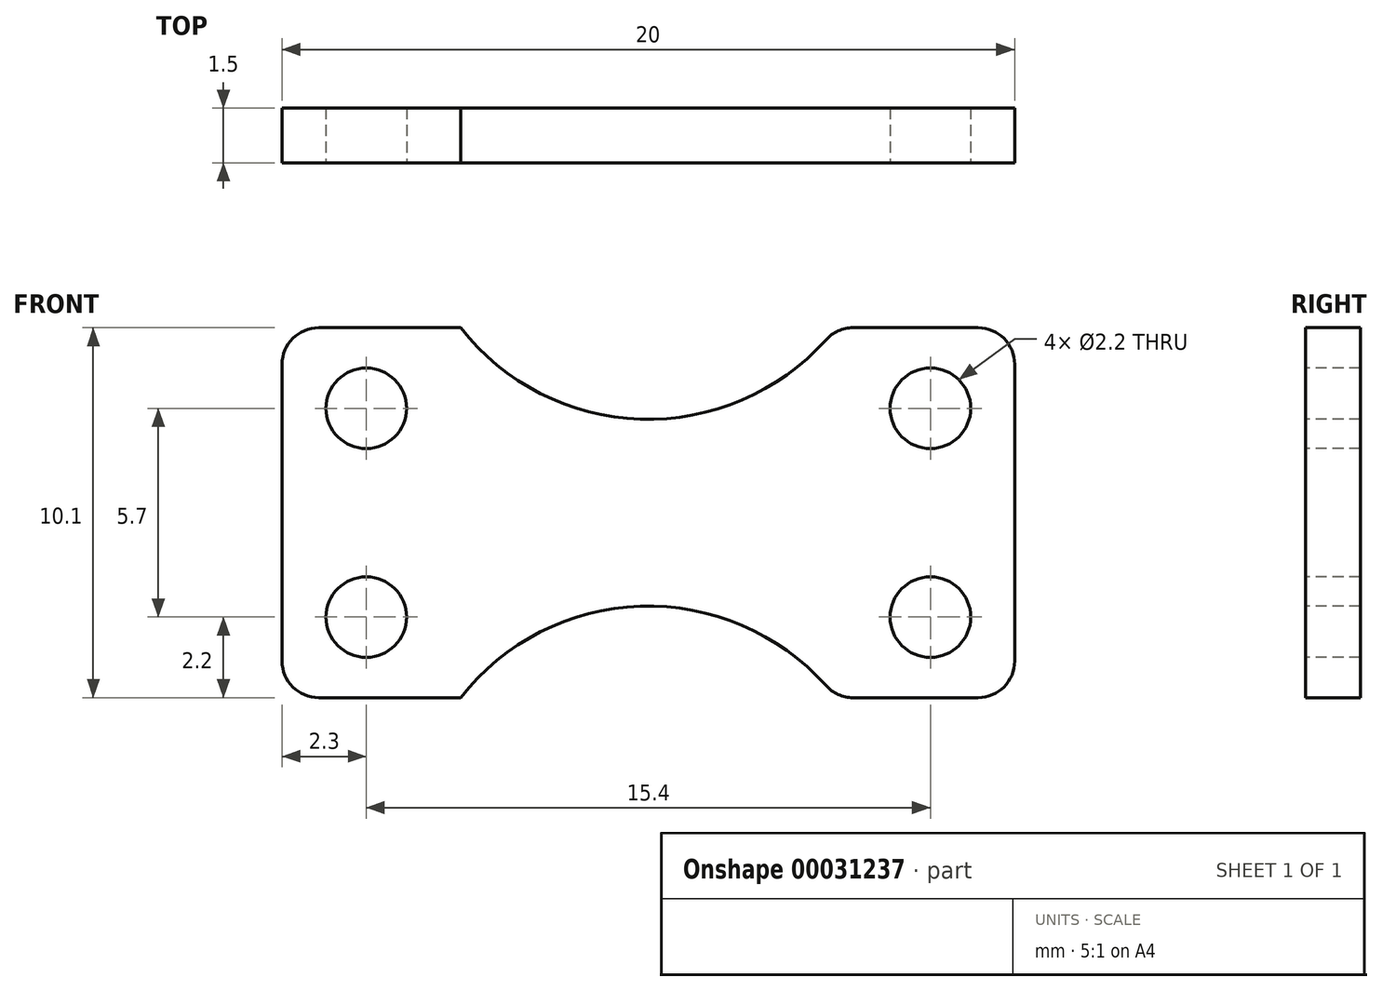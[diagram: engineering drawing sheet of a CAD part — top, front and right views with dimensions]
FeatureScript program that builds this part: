
annotation { "Feature Type Name" : "Feature", "Feature Type Description" : "" }
export const myFeature = defineFeature(function(context is Context, id is Id, definition is map)
    precondition{}
    {
        {
            var Q0;
            Q0=qCreatedBy(makeId("Front.planeOp"),FACE);
            var sketch = newSketch(context, id + "F0", { "sketchPlane" : qUnion([Q0])});
            skLineSegment(sketch, "E0.bottom", {"start": v(0, 0) * mm, "end": v(20, 0) * mm});
            skLineSegment(sketch, "E0.top", {"start": v(0, 10.1) * mm, "end": v(20, 10.1) * mm});
            skLineSegment(sketch, "E0.left", {"start": v(0, 0) * mm, "end": v(0, 10.1) * mm});
            skLineSegment(sketch, "E0.right", {"start": v(20, 0) * mm, "end": v(20, 10.1) * mm});
            skSolve(sketch);
        }
        {
            var Q0;
            Q0=qSketchRegion(id+"F0",true);
            extrude(context, id + "F1", {"entities" : qUnion([Q0]), "depth" : 1.5 * mm});
        }
        {
            var Q0;
            Q0=makeQuery(id+"F1.opExtrude","CAP_FACE",FACE,{"disambiguationData":[OSD([sQuery(id+"F0.wireOp",EDGE,"E0.bottom"),sQuery(id+"F0.wireOp",EDGE,"E0.top"),sQuery(id+"F0.wireOp",EDGE,"E0.left"),sQuery(id+"F0.wireOp",EDGE,"E0.right")])],"isStart":false});
            var sketch = newSketch(context, id + "F2", { "sketchPlane" : qUnion([Q0])});
            skLineSegment(sketch, "E1", {"start": v(0, 5.05) * mm, "end": v(20, 5.05) * mm, "construction": true});
            skLineSegment(sketch, "E2", {"start": v(10, 10.1) * mm, "end": v(10, 0) * mm, "construction": true});
            skPoint(sketch, "E3", {"position": v(10, 5.05) * mm});
            skCircle(sketch, "E4", {"center": v(2.3, 7.9) * mm, "radius": 1.1 * mm});
            skCircle(sketch, "E5.MirrorC", {"center": v(17.7, 7.9) * mm, "radius": 1.1 * mm});
            skCircle(sketch, "E6.MirrorC", {"center": v(2.3, 2.2) * mm, "radius": 1.1 * mm});
            skCircle(sketch, "E7.MirrorC", {"center": v(17.7, 2.2) * mm, "radius": 1.1 * mm});
            skLineSegment(sketch, "E8", {"start": v(0, 14.1) * mm, "end": v(19.96, 14.1) * mm, "construction": true});
            skPoint(sketch, "E9", {"position": v(10, 14.1) * mm});
            skArc(sketch, "E10", {"start": v(4.88, 10.1) * mm, "mid": v(10, 7.6) * mm, "end": v(15.12, 10.1) * mm});
            skLineSegment(sketch, "E11", {"start": v(4.88, 10.1) * mm, "end": v(15.12, 10.1) * mm});
            skArc(sketch, "E12.MirrorCS", {"start": v(4.88, 0) * mm, "mid": v(10, 2.5) * mm, "end": v(15.12, 0) * mm});
            skLineSegment(sketch, "E13.MirrorCS", {"start": v(4.88, 0) * mm, "end": v(15.12, 0) * mm});
            skSolve(sketch);
        }
        {
            var Q0;
            Q0=qSketchRegion(id+"F2",true);
            extrude(context, id + "F3", {"entities" : qUnion([Q0]), "operationType" : NewBodyOperationType.REMOVE, "endBound" : BoundingType.UP_TO_NEXT, "oppositeDirection" : true, "depth" : 25 * mm});
        }
        {
            var Q0;
            Q0=makeQuery(id+"F1.opExtrude","SWEPT_EDGE",EDGE,{"disambiguationData":[OSD([sQuery(id+"F0.wireOp",EDGE,"E0.top"),sQuery(id+"F0.wireOp",EDGE,"E0.right")])]});
            var Q1;
            Q1=makeQuery(id+"F1.opExtrude","SWEPT_EDGE",EDGE,{"disambiguationData":[OSD([sQuery(id+"F0.wireOp",EDGE,"E0.bottom"),sQuery(id+"F0.wireOp",EDGE,"E0.right")])]});
            var Q2;
            Q2=makeQuery(id+"F1.opExtrude","SWEPT_EDGE",EDGE,{"disambiguationData":[OSD([sQuery(id+"F0.wireOp",EDGE,"E0.top"),sQuery(id+"F0.wireOp",EDGE,"E0.left")])]});
            var Q3;
            Q3=makeQuery(id+"F1.opExtrude","SWEPT_EDGE",EDGE,{"disambiguationData":[OSD([sQuery(id+"F0.wireOp",EDGE,"E0.bottom"),sQuery(id+"F0.wireOp",EDGE,"E0.left")])]});
            var Q4;
            {var subQ0=sQuery(id+"F0.wireOp",EDGE,"E0.top");var subQ1=sQuery(id+"F2.wireOp",EDGE,"E10");var subQ2=sQuery(id+"F2.wireOp",EDGE,"E11");Q4=makeQuery(id+"F3.boolean.opBoolean","COPY",EDGE,{"derivedFrom":makeQuery(id+"F3.opExtrude","SWEPT_EDGE",EDGE,{"disambiguationData":[OSD([subQ0,subQ1,subQ2]),TDD([makeQuery(id+"F2.imprint","INTERSECT",VERTEX,{"disambiguationData":[OD(0.0)],"derivedFrom":[makeQuery(id+"F1.opExtrude","CAP_EDGE",EDGE,{"disambiguationData":[OSD([subQ0])],"isStart":false}),subQ1,subQ2]})])]})});}
            var Q5;
            {var subQ0=sQuery(id+"F0.wireOp",EDGE,"E0.top");var subQ1=sQuery(id+"F2.wireOp",EDGE,"E10");var subQ2=sQuery(id+"F2.wireOp",EDGE,"E11");Q5=makeQuery(id+"F3.boolean.opBoolean","COPY",EDGE,{"derivedFrom":makeQuery(id+"F3.opExtrude","SWEPT_EDGE",EDGE,{"disambiguationData":[OSD([subQ0,subQ1,subQ2]),TDD([makeQuery(id+"F2.imprint","INTERSECT",VERTEX,{"disambiguationData":[OD(1.0)],"derivedFrom":[makeQuery(id+"F1.opExtrude","CAP_EDGE",EDGE,{"disambiguationData":[OSD([subQ0])],"isStart":false}),subQ1,subQ2]})])]})});}
            var Q6;
            {var subQ0=sQuery(id+"F0.wireOp",EDGE,"E0.bottom");var subQ1=sQuery(id+"F2.wireOp",EDGE,"E12.MirrorCS");var subQ2=sQuery(id+"F2.wireOp",EDGE,"E13.MirrorCS");Q6=makeQuery(id+"F3.boolean.opBoolean","COPY",EDGE,{"derivedFrom":makeQuery(id+"F3.opExtrude","SWEPT_EDGE",EDGE,{"disambiguationData":[OSD([subQ0,subQ1,subQ2]),TDD([makeQuery(id+"F2.imprint","INTERSECT",VERTEX,{"disambiguationData":[OD(0.0)],"derivedFrom":[makeQuery(id+"F1.opExtrude","CAP_EDGE",EDGE,{"disambiguationData":[OSD([subQ0])],"isStart":false}),subQ1,subQ2]})])]})});}
            var Q7;
            {var subQ0=sQuery(id+"F0.wireOp",EDGE,"E0.bottom");var subQ1=sQuery(id+"F2.wireOp",EDGE,"E12.MirrorCS");var subQ2=sQuery(id+"F2.wireOp",EDGE,"E13.MirrorCS");Q7=makeQuery(id+"F3.boolean.opBoolean","COPY",EDGE,{"derivedFrom":makeQuery(id+"F3.opExtrude","SWEPT_EDGE",EDGE,{"disambiguationData":[OSD([subQ0,subQ1,subQ2]),TDD([makeQuery(id+"F2.imprint","INTERSECT",VERTEX,{"disambiguationData":[OD(1.0)],"derivedFrom":[makeQuery(id+"F1.opExtrude","CAP_EDGE",EDGE,{"disambiguationData":[OSD([subQ0])],"isStart":false}),subQ1,subQ2]})])]})});}
            fillet(context, id + "F4", {"entities" : qUnion([Q0, Q1, Q2, Q3, Q4, Q5, Q6, Q7]), "radius" : 1 * mm, "tangentPropagation" : true, "allowEdgeOverflow" : false});
        }
    });
